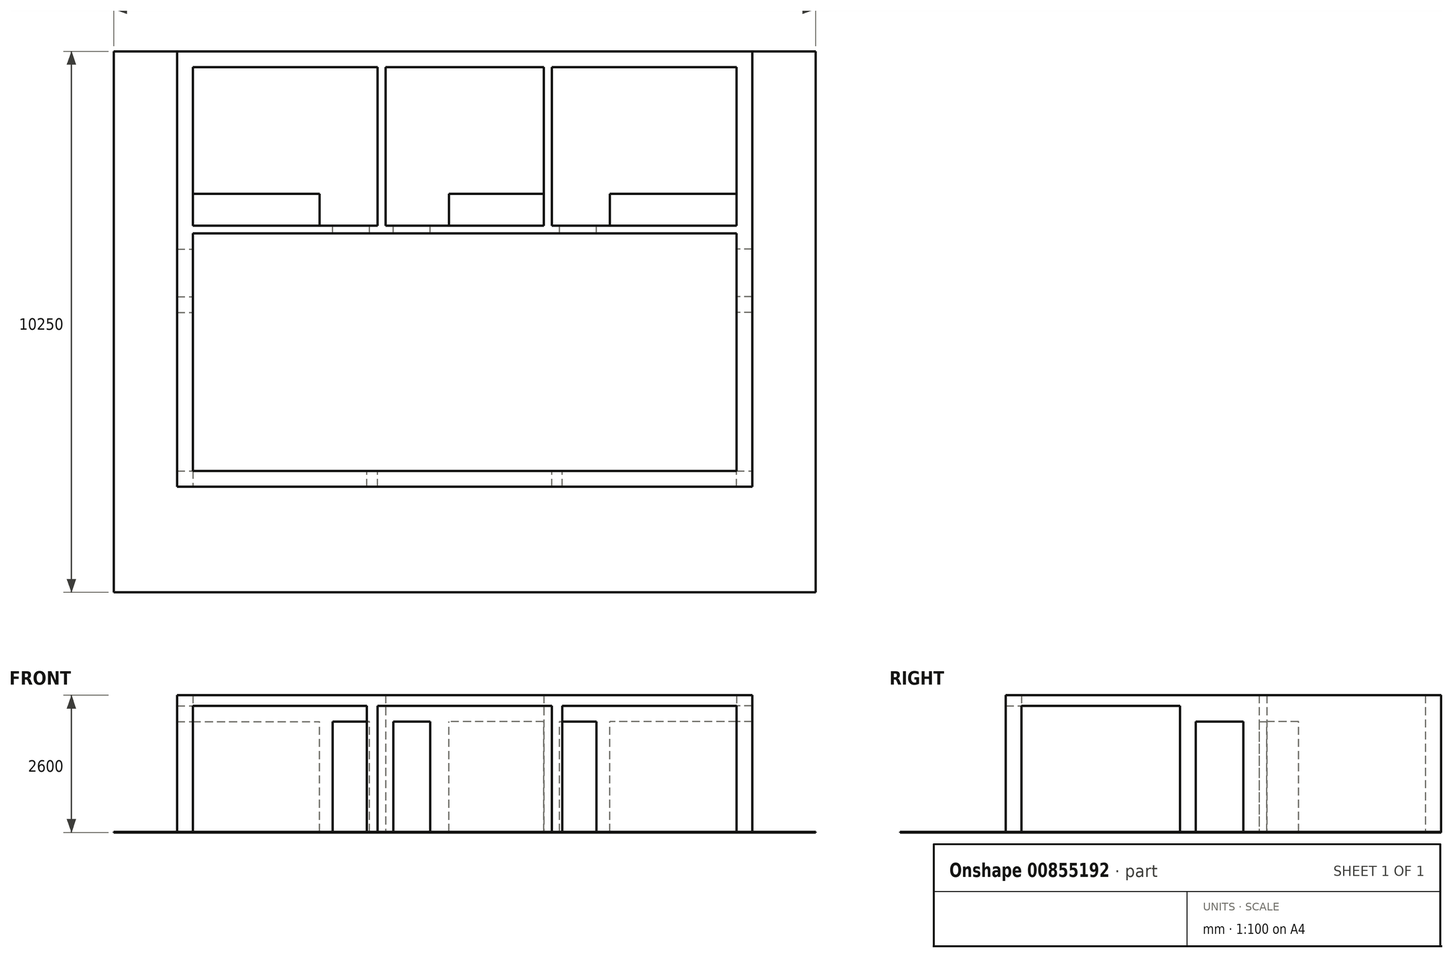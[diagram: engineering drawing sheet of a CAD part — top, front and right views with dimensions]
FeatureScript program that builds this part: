
annotation { "Feature Type Name" : "Feature", "Feature Type Description" : "" }
export const myFeature = defineFeature(function(context is Context, id is Id, definition is map)
    precondition{}
    {
        {
            var Q0;
            Q0=qCreatedBy(makeId("Top.planeOp"),FACE);
            var sketch = newSketch(context, id + "F0", { "sketchPlane" : qUnion([Q0])});
            skLineSegment(sketch, "E0.bottom", {"start": v(0, 0) * mm, "end": v(3500, 0) * mm});
            skLineSegment(sketch, "E0.top", {"start": v(0, 3000) * mm, "end": v(3500, 3000) * mm});
            skLineSegment(sketch, "E0.left", {"start": v(0, 0) * mm, "end": v(0, 3000) * mm});
            skLineSegment(sketch, "E0.right", {"start": v(3500, 0) * mm, "end": v(3500, 3000) * mm});
            skLineSegment(sketch, "E1.bottom", {"start": v(3650, 0) * mm, "end": v(6650, 0) * mm});
            skLineSegment(sketch, "E1.top", {"start": v(3650, 3000) * mm, "end": v(6650, 3000) * mm});
            skLineSegment(sketch, "E1.left", {"start": v(3650, 0) * mm, "end": v(3650, 3000) * mm});
            skLineSegment(sketch, "E1.right", {"start": v(6650, 0) * mm, "end": v(6650, 3000) * mm});
            skLineSegment(sketch, "E2.bottom", {"start": v(6800, 0) * mm, "end": v(10300, 0) * mm});
            skLineSegment(sketch, "E2.top", {"start": v(6800, 3000) * mm, "end": v(10300, 3000) * mm});
            skLineSegment(sketch, "E2.left", {"start": v(6800, 0) * mm, "end": v(6800, 3000) * mm});
            skLineSegment(sketch, "E2.right", {"start": v(10300, 0) * mm, "end": v(10300, 3000) * mm});
            skLineSegment(sketch, "E3.bottom", {"start": v(0, -150) * mm, "end": v(10300, -150) * mm});
            skLineSegment(sketch, "E3.top", {"start": v(0, -4650) * mm, "end": v(10300, -4650) * mm});
            skLineSegment(sketch, "E3.left", {"start": v(0, -150) * mm, "end": v(0, -4650) * mm});
            skLineSegment(sketch, "E3.right", {"start": v(10300, -150) * mm, "end": v(10300, -4650) * mm});
            skLineSegment(sketch, "E4.bottom", {"start": v(-300, -4950) * mm, "end": v(10600, -4950) * mm});
            skLineSegment(sketch, "E4.top", {"start": v(-300, 3300) * mm, "end": v(10600, 3300) * mm});
            skLineSegment(sketch, "E4.left", {"start": v(-300, -4950) * mm, "end": v(-300, 3300) * mm});
            skLineSegment(sketch, "E4.right", {"start": v(10600, -4950) * mm, "end": v(10600, 3300) * mm});
            skSolve(sketch);
        }
        {
            var Q0;
            Q0=makeQuery(id+"F0.imprint","IMPRINT",FACE,{"disambiguationData":[TD([[makeQuery(id+"F0.imprint","IMPRINT",EDGE,{"derivedFrom":sQuery(id+"F0.wireOp",EDGE,"E0.bottom")}),-1.0]])]});
            extrude(context, id + "F1", {"entities" : qUnion([Q0]), "depth" : 2600 * mm, "offsetDistance" : 25 * mm});
        }
        {
            var Q0;
            Q0=makeQuery(id+"F1.opExtrude","SWEPT_FACE",FACE,{"disambiguationData":[OSD([sQuery(id+"F0.wireOp",EDGE,"E0.bottom")])]});
            var sketch = newSketch(context, id + "F2", { "sketchPlane" : qUnion([Q0])});
            skLineSegment(sketch, "E5.bottom", {"start": v(-3350, 0) * mm, "end": v(-2650, 0) * mm});
            skLineSegment(sketch, "E5.top", {"start": v(-3350, 2100) * mm, "end": v(-2650, 2100) * mm});
            skLineSegment(sketch, "E5.left", {"start": v(-3350, 0) * mm, "end": v(-3350, 2100) * mm});
            skLineSegment(sketch, "E5.right", {"start": v(-2650, 0) * mm, "end": v(-2650, 2100) * mm});
            skLineSegment(sketch, "E6.bottom", {"start": v(-7650, 0) * mm, "end": v(-6950, 0) * mm});
            skLineSegment(sketch, "E6.top", {"start": v(-7650, 2100) * mm, "end": v(-6950, 2100) * mm});
            skLineSegment(sketch, "E6.left", {"start": v(-7650, 0) * mm, "end": v(-7650, 2100) * mm});
            skLineSegment(sketch, "E6.right", {"start": v(-6950, 0) * mm, "end": v(-6950, 2100) * mm});
            skLineSegment(sketch, "E7.bottom", {"start": v(-4500, 0) * mm, "end": v(-3800, 0) * mm});
            skLineSegment(sketch, "E7.top", {"start": v(-4500, 2100) * mm, "end": v(-3800, 2100) * mm});
            skLineSegment(sketch, "E7.left", {"start": v(-4500, 0) * mm, "end": v(-4500, 2100) * mm});
            skLineSegment(sketch, "E7.right", {"start": v(-3800, 0) * mm, "end": v(-3800, 2100) * mm});
            skSolve(sketch);
        }
        {
            var Q0;
            Q0=makeQuery(id+"F2.imprint","IMPRINT",FACE,{"disambiguationData":[TD([[makeQuery(id+"F2.imprint","IMPRINT",EDGE,{"derivedFrom":sQuery(id+"F2.wireOp",EDGE,"E7.bottom")}),1.0]])]});
            var Q1;
            Q1=makeQuery(id+"F2.imprint","IMPRINT",FACE,{"disambiguationData":[TD([[makeQuery(id+"F2.imprint","IMPRINT",EDGE,{"derivedFrom":sQuery(id+"F2.wireOp",EDGE,"E6.bottom")}),1.0]])]});
            var Q2;
            Q2=makeQuery(id+"F2.imprint","IMPRINT",FACE,{"disambiguationData":[TD([[makeQuery(id+"F2.imprint","IMPRINT",EDGE,{"derivedFrom":sQuery(id+"F2.wireOp",EDGE,"E5.bottom")}),-1.0]])]});
            extrude(context, id + "F3", {"entities" : qUnion([Q0, Q1, Q2]), "operationType" : NewBodyOperationType.REMOVE, "endBound" : BoundingType.UP_TO_NEXT, "oppositeDirection" : true, "depth" : 25 * mm, "offsetDistance" : 25 * mm});
        }
        {
            var Q0;
            Q0=makeQuery(id+"F1.opExtrude","SWEPT_FACE",FACE,{"disambiguationData":[OSD([sQuery(id+"F0.wireOp",EDGE,"E0.bottom")])]});
            var sketch = newSketch(context, id + "F4", { "sketchPlane" : qUnion([Q0])});
            skLineSegment(sketch, "E8.bottom", {"start": v(0, 0) * mm, "end": v(-2400, 0) * mm});
            skLineSegment(sketch, "E8.top", {"start": v(0, 2100) * mm, "end": v(-2400, 2100) * mm});
            skLineSegment(sketch, "E8.left", {"start": v(0, 0) * mm, "end": v(0, 2100) * mm});
            skLineSegment(sketch, "E8.right", {"start": v(-2400, 0) * mm, "end": v(-2400, 2100) * mm});
            skPoint(sketch, "E9.oppositeSnap0", {"position": v(-3000, 2100) * mm});
            skLineSegment(sketch, "E9.bottom", {"start": v(-10300, 0) * mm, "end": v(-7900, 0) * mm});
            skLineSegment(sketch, "E9.top", {"start": v(-10300, 2100) * mm, "end": v(-7900, 2100) * mm});
            skLineSegment(sketch, "E9.left", {"start": v(-10300, 0) * mm, "end": v(-10300, 2100) * mm});
            skLineSegment(sketch, "E9.right", {"start": v(-7900, 0) * mm, "end": v(-7900, 2100) * mm});
            skLineSegment(sketch, "E10.bottom", {"start": v(-6650, 0) * mm, "end": v(-4850, 0) * mm});
            skLineSegment(sketch, "E10.top", {"start": v(-6650, 2100) * mm, "end": v(-4850, 2100) * mm});
            skLineSegment(sketch, "E10.left", {"start": v(-6650, 0) * mm, "end": v(-6650, 2100) * mm});
            skLineSegment(sketch, "E10.right", {"start": v(-4850, 0) * mm, "end": v(-4850, 2100) * mm});
            skSolve(sketch);
        }
        {
            var Q0;
            Q0=makeQuery(id+"F4.imprint","IMPRINT",FACE,{"disambiguationData":[TD([[makeQuery(id+"F4.imprint","IMPRINT",EDGE,{"derivedFrom":sQuery(id+"F4.wireOp",EDGE,"E9.bottom")}),1.0]])]});
            var Q1;
            Q1=makeQuery(id+"F4.imprint","IMPRINT",FACE,{"disambiguationData":[TD([[makeQuery(id+"F4.imprint","IMPRINT",EDGE,{"derivedFrom":sQuery(id+"F4.wireOp",EDGE,"E10.bottom")}),1.0]])]});
            var Q2;
            Q2=makeQuery(id+"F4.imprint","IMPRINT",FACE,{"disambiguationData":[TD([[makeQuery(id+"F4.imprint","IMPRINT",EDGE,{"derivedFrom":sQuery(id+"F4.wireOp",EDGE,"E8.bottom")}),-1.0]])]});
            extrude(context, id + "F5", {"entities" : qUnion([Q0, Q1, Q2]), "operationType" : NewBodyOperationType.ADD, "depth" : 600 * mm, "offsetDistance" : 25 * mm});
        }
        {
            var Q0;
            Q0=makeQuery(id+"F1.opExtrude","SWEPT_FACE",FACE,{"disambiguationData":[OSD([sQuery(id+"F0.wireOp",EDGE,"E3.right")])]});
            var sketch = newSketch(context, id + "F6", { "sketchPlane" : qUnion([Q0])});
            skLineSegment(sketch, "E11.bottom", {"start": v(450, 0) * mm, "end": v(1350, 0) * mm});
            skLineSegment(sketch, "E11.top", {"start": v(450, 2100) * mm, "end": v(1350, 2100) * mm});
            skLineSegment(sketch, "E11.left", {"start": v(450, 0) * mm, "end": v(450, 2100) * mm});
            skLineSegment(sketch, "E11.right", {"start": v(1350, 0) * mm, "end": v(1350, 2100) * mm});
            skSolve(sketch);
        }
        {
            var Q0;
            Q0=makeQuery(id+"F6.imprint","IMPRINT",FACE,{"disambiguationData":[TD([[makeQuery(id+"F6.imprint","IMPRINT",EDGE,{"derivedFrom":sQuery(id+"F6.wireOp",EDGE,"E11.bottom")}),1.0]])]});
            extrude(context, id + "F7", {"entities" : qUnion([Q0]), "operationType" : NewBodyOperationType.REMOVE, "endBound" : BoundingType.UP_TO_NEXT, "oppositeDirection" : true, "depth" : 25 * mm, "offsetDistance" : 25 * mm});
        }
        {
            var Q0;
            Q0=makeQuery(id+"F1.opExtrude","SWEPT_FACE",FACE,{"disambiguationData":[OSD([sQuery(id+"F0.wireOp",EDGE,"E3.left")])]});
            var sketch = newSketch(context, id + "F8", { "sketchPlane" : qUnion([Q0])});
            skLineSegment(sketch, "E12.bottom", {"start": v(-450, 0) * mm, "end": v(-1350, 0) * mm});
            skLineSegment(sketch, "E12.top", {"start": v(-450, 2100) * mm, "end": v(-1350, 2100) * mm});
            skLineSegment(sketch, "E12.left", {"start": v(-450, 0) * mm, "end": v(-450, 2100) * mm});
            skLineSegment(sketch, "E12.right", {"start": v(-1350, 0) * mm, "end": v(-1350, 2100) * mm});
            skSolve(sketch);
        }
        {
            var Q0;
            Q0=makeQuery(id+"F8.imprint","IMPRINT",FACE,{"disambiguationData":[TD([[makeQuery(id+"F8.imprint","IMPRINT",EDGE,{"derivedFrom":sQuery(id+"F8.wireOp",EDGE,"E12.bottom")}),-1.0]])]});
            extrude(context, id + "F9", {"entities" : qUnion([Q0]), "operationType" : NewBodyOperationType.REMOVE, "endBound" : BoundingType.UP_TO_NEXT, "oppositeDirection" : true, "depth" : 25 * mm, "offsetDistance" : 25 * mm});
        }
        {
            var Q0;
            Q0=makeQuery(id+"F1.opExtrude","SWEPT_FACE",FACE,{"disambiguationData":[OSD([sQuery(id+"F0.wireOp",EDGE,"E3.right")])]});
            var sketch = newSketch(context, id + "F10", { "sketchPlane" : qUnion([Q0])});
            skLineSegment(sketch, "E13.bottom", {"start": v(1650, 0) * mm, "end": v(4650, 0) * mm});
            skLineSegment(sketch, "E13.top", {"start": v(1650, 2400) * mm, "end": v(4650, 2400) * mm});
            skLineSegment(sketch, "E13.left", {"start": v(1650, 0) * mm, "end": v(1650, 2400) * mm});
            skLineSegment(sketch, "E13.right", {"start": v(4650, 0) * mm, "end": v(4650, 2400) * mm});
            skSolve(sketch);
        }
        {
            var Q0;
            Q0=makeQuery(id+"F1.opExtrude","SWEPT_FACE",FACE,{"disambiguationData":[OSD([sQuery(id+"F0.wireOp",EDGE,"E3.left")])]});
            var sketch = newSketch(context, id + "F11", { "sketchPlane" : qUnion([Q0])});
            skLineSegment(sketch, "E14.bottom", {"start": v(-4650, 0) * mm, "end": v(-1650, 0) * mm});
            skLineSegment(sketch, "E14.top", {"start": v(-4650, 2400) * mm, "end": v(-1650, 2400) * mm});
            skLineSegment(sketch, "E14.left", {"start": v(-4650, 0) * mm, "end": v(-4650, 2400) * mm});
            skLineSegment(sketch, "E14.right", {"start": v(-1650, 0) * mm, "end": v(-1650, 2400) * mm});
            skSolve(sketch);
        }
        {
            var Q0;
            Q0=makeQuery(id+"F11.imprint","IMPRINT",FACE,{"disambiguationData":[TD([[makeQuery(id+"F11.imprint","IMPRINT",EDGE,{"derivedFrom":sQuery(id+"F11.wireOp",EDGE,"E14.bottom")}),-1.0]])]});
            extrude(context, id + "F12", {"entities" : qUnion([Q0]), "operationType" : NewBodyOperationType.REMOVE, "endBound" : BoundingType.UP_TO_NEXT, "oppositeDirection" : true, "depth" : 25 * mm, "offsetDistance" : 25 * mm});
        }
        {
            var Q0;
            Q0=makeQuery(id+"F10.imprint","IMPRINT",FACE,{"disambiguationData":[TD([[makeQuery(id+"F10.imprint","IMPRINT",EDGE,{"derivedFrom":sQuery(id+"F10.wireOp",EDGE,"E13.bottom")}),1.0]])]});
            extrude(context, id + "F13", {"entities" : qUnion([Q0]), "operationType" : NewBodyOperationType.REMOVE, "endBound" : BoundingType.UP_TO_NEXT, "oppositeDirection" : true, "depth" : 25 * mm, "offsetDistance" : 25 * mm});
        }
        {
            var Q0;
            Q0=makeQuery(id+"F13.boolean.opBoolean","MERGE",FACE,{"derivedFrom":[makeQuery(id+"F12.boolean.opBoolean","MERGE",FACE,{"derivedFrom":[makeQuery(id+"F1.opExtrude","SWEPT_FACE",FACE,{"disambiguationData":[OSD([sQuery(id+"F0.wireOp",EDGE,"E3.top")])]}),makeQuery(id+"F12.opExtrude","SWEPT_FACE",FACE,{"disambiguationData":[OSD([sQuery(id+"F11.wireOp",EDGE,"E14.left")])]})]}),makeQuery(id+"F13.opExtrude","SWEPT_FACE",FACE,{"disambiguationData":[OSD([sQuery(id+"F10.wireOp",EDGE,"E13.right")])]})]});
            var sketch = newSketch(context, id + "F14", { "sketchPlane" : qUnion([Q0])});
            skLineSegment(sketch, "E15.bottom", {"start": v(-10300, 2400) * mm, "end": v(-7000, 2400) * mm});
            skLineSegment(sketch, "E15.top", {"start": v(-10300, 0) * mm, "end": v(-7000, 0) * mm});
            skLineSegment(sketch, "E15.left", {"start": v(-10300, 2400) * mm, "end": v(-10300, 0) * mm});
            skLineSegment(sketch, "E15.right", {"start": v(-7000, 2400) * mm, "end": v(-7000, 0) * mm});
            skLineSegment(sketch, "E16.bottom", {"start": v(0, 2400) * mm, "end": v(-3300, 2400) * mm});
            skLineSegment(sketch, "E16.top", {"start": v(0, 0) * mm, "end": v(-3300, 0) * mm});
            skLineSegment(sketch, "E16.left", {"start": v(0, 2400) * mm, "end": v(0, 0) * mm});
            skLineSegment(sketch, "E16.right", {"start": v(-3300, 2400) * mm, "end": v(-3300, 0) * mm});
            skLineSegment(sketch, "E17.bottom", {"start": v(-6800, 0) * mm, "end": v(-3500, 0) * mm});
            skLineSegment(sketch, "E17.top", {"start": v(-6800, 2400) * mm, "end": v(-3500, 2400) * mm});
            skLineSegment(sketch, "E17.left", {"start": v(-6800, 0) * mm, "end": v(-6800, 2400) * mm});
            skLineSegment(sketch, "E17.right", {"start": v(-3500, 0) * mm, "end": v(-3500, 2400) * mm});
            skSolve(sketch);
        }
        {
            var Q0;
            Q0=makeQuery(id+"F14.imprint","IMPRINT",FACE,{"disambiguationData":[TD([[makeQuery(id+"F14.imprint","IMPRINT",EDGE,{"derivedFrom":sQuery(id+"F14.wireOp",EDGE,"E15.bottom")}),-1.0]])]});
            var Q1;
            Q1=makeQuery(id+"F14.imprint","IMPRINT",FACE,{"disambiguationData":[TD([[makeQuery(id+"F14.imprint","IMPRINT",EDGE,{"derivedFrom":sQuery(id+"F14.wireOp",EDGE,"E17.bottom")}),-1.0]])]});
            var Q2;
            Q2=makeQuery(id+"F14.imprint","IMPRINT",FACE,{"disambiguationData":[TD([[makeQuery(id+"F14.imprint","IMPRINT",EDGE,{"derivedFrom":sQuery(id+"F14.wireOp",EDGE,"E16.bottom")}),1.0]])]});
            extrude(context, id + "F15", {"entities" : qUnion([Q0, Q1, Q2]), "operationType" : NewBodyOperationType.REMOVE, "endBound" : BoundingType.UP_TO_NEXT, "oppositeDirection" : true, "depth" : 25 * mm, "offsetDistance" : 25 * mm});
        }
        {
            var Q0;
            Q0=qCreatedBy(makeId("Top.planeOp"),FACE);
            var sketch = newSketch(context, id + "F16", { "sketchPlane" : qUnion([Q0])});
            skLineSegment(sketch, "E18.bottom", {"start": v(-1500, -6950) * mm, "end": v(11800, -6950) * mm});
            skLineSegment(sketch, "E18.top", {"start": v(-1500, 3300) * mm, "end": v(11800, 3300) * mm});
            skLineSegment(sketch, "E18.left", {"start": v(-1500, -6950) * mm, "end": v(-1500, 3300) * mm});
            skLineSegment(sketch, "E18.right", {"start": v(11800, -6950) * mm, "end": v(11800, 3300) * mm});
            skSolve(sketch);
        }
        {
            var Q0;
            Q0=makeQuery(id+"F16.imprint","IMPRINT",FACE,{"disambiguationData":[TD([[makeQuery(id+"F16.imprint","IMPRINT",EDGE,{"derivedFrom":sQuery(id+"F16.wireOp",EDGE,"E18.bottom")}),1.0]])]});
            extrude(context, id + "F17", {"entities" : qUnion([Q0]), "operationType" : NewBodyOperationType.ADD, "depth" : 10 * mm, "offsetDistance" : 25 * mm});
        }
    });
